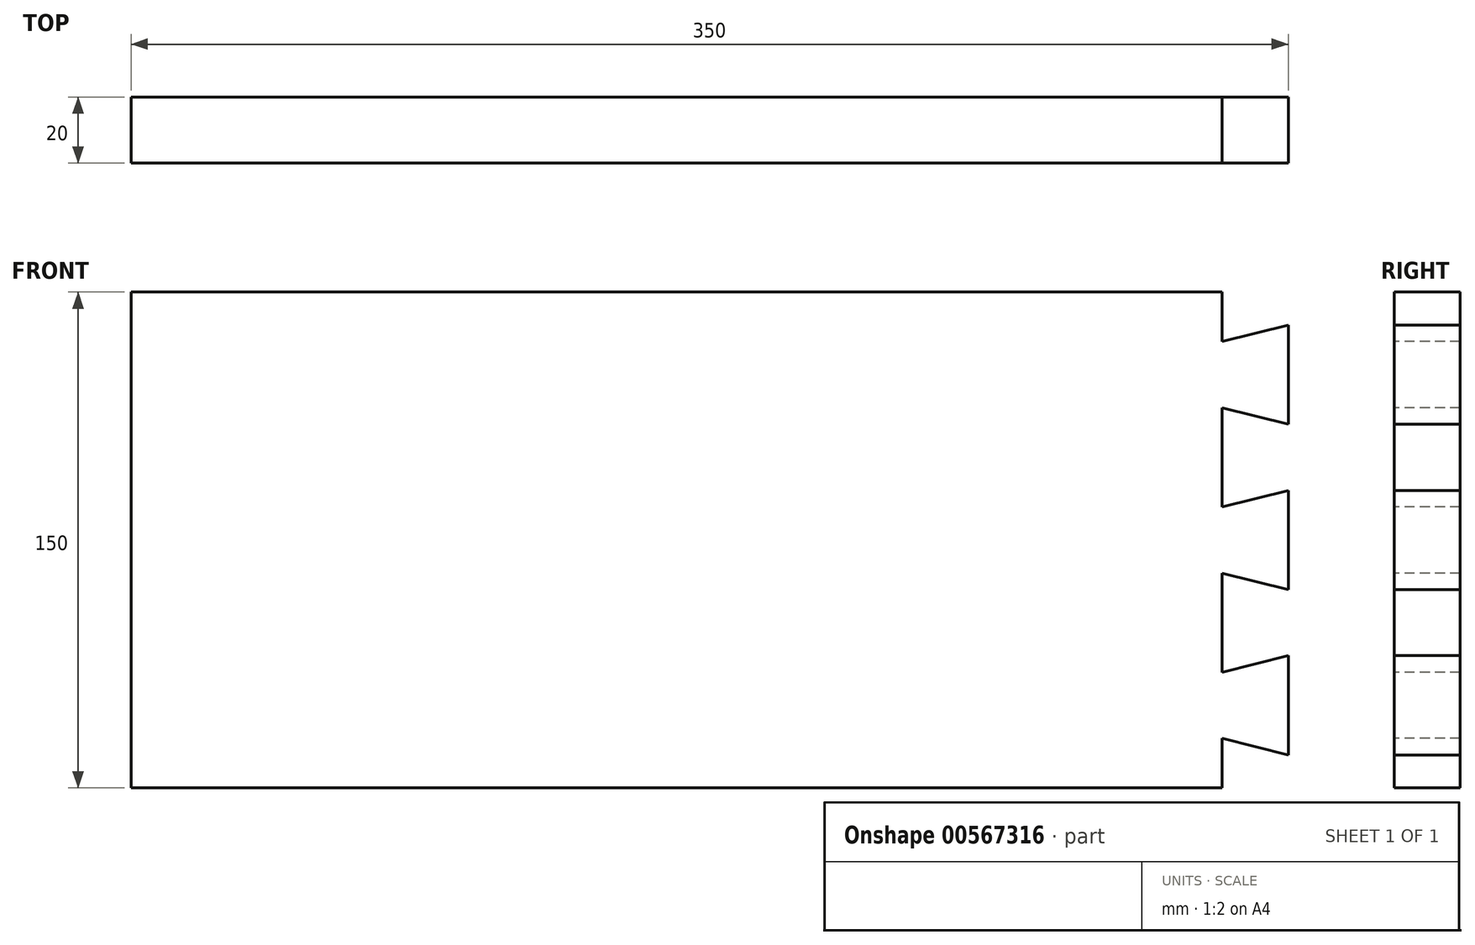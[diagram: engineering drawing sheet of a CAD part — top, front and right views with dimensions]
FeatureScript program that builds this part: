
annotation { "Feature Type Name" : "Feature", "Feature Type Description" : "" }
export const myFeature = defineFeature(function(context is Context, id is Id, definition is map)
    precondition{}
    {
        {
            var Q0;
            Q0=qCreatedBy(makeId("Front.planeOp"),FACE);
            var sketch = newSketch(context, id + "F0", { "sketchPlane" : qUnion([Q0])});
            skLineSegment(sketch, "E0.bottom", {"start": v(-187.02, 82.7) * mm, "end": v(162.98, 82.7) * mm});
            skLineSegment(sketch, "E0.top", {"start": v(-187.02, -67.3) * mm, "end": v(162.98, -67.3) * mm});
            skLineSegment(sketch, "E0.left", {"start": v(-187.02, 82.7) * mm, "end": v(-187.02, -67.3) * mm});
            skLineSegment(sketch, "E0.right", {"start": v(162.98, 82.7) * mm, "end": v(162.98, -67.3) * mm});
            skSolve(sketch);
        }
        {
            var Q0;
            Q0 = qSketchRegion(id + "F0", true);
            extrude(context, id + "F1", {"entities" : qUnion([Q0]), "depth" : 20 * mm, "offsetDistance" : 25 * mm});
        }
        {
            var Q0;
            Q0=makeQuery(id+"F1.opExtrude","SWEPT_FACE",FACE,{"disambiguationData":[OSD([sQuery(id+"F0.wireOp",EDGE,"E0.right")])]});
            var sketch = newSketch(context, id + "F2", { "sketchPlane" : qUnion([Q0])});
            skLineSegment(sketch, "E1", {"start": v(-20, 7.7) * mm, "end": v(0, 7.7) * mm});
            skLineSegment(sketch, "E2", {"start": v(-20, 22.7) * mm, "end": v(0, 17.7) * mm});
            skLineSegment(sketch, "E3", {"start": v(0, -2.3) * mm, "end": v(-20, -7.3) * mm});
            skLineSegment(sketch, "E4", {"start": v(-20, 42.7) * mm, "end": v(0, 47.7) * mm});
            skLineSegment(sketch, "E5", {"start": v(-20, 72.7) * mm, "end": v(0, 67.7) * mm});
            skLineSegment(sketch, "E6", {"start": v(-20, -27.3) * mm, "end": v(0, -32.3) * mm});
            skLineSegment(sketch, "E7", {"start": v(-20, -57.3) * mm, "end": v(0, -52.3) * mm});
            skSolve(sketch);
        }
        {
            var Q0;
            {var subQ0=sQuery(id+"F2.wireOp",EDGE,"E5");Q0=makeQuery(id+"F2.imprint","IMPRINT",FACE,{"disambiguationData":[TD([[makeQuery(id+"F2.imprint","IMPRINT",EDGE,{"derivedFrom":subQ0}),1.0]])]});}
            var Q1;
            {var subQ0=sQuery(id+"F2.wireOp",EDGE,"E2");Q1=makeQuery(id+"F2.imprint","IMPRINT",FACE,{"disambiguationData":[TD([[makeQuery(id+"F2.imprint","IMPRINT",EDGE,{"derivedFrom":subQ0}),1.0]])]});}
            var Q2;
            {var subQ0=sQuery(id+"F2.wireOp",EDGE,"E3");Q2=makeQuery(id+"F2.imprint","IMPRINT",FACE,{"disambiguationData":[TD([[makeQuery(id+"F2.imprint","IMPRINT",EDGE,{"derivedFrom":subQ0}),1.0]])]});}
            var Q3;
            {var subQ0=sQuery(id+"F2.wireOp",EDGE,"E7");Q3=makeQuery(id+"F2.imprint","IMPRINT",FACE,{"disambiguationData":[TD([[makeQuery(id+"F2.imprint","IMPRINT",EDGE,{"derivedFrom":subQ0}),-1.0]])]});}
            extrude(context, id + "F3", {"entities" : qUnion([Q0, Q1, Q2, Q3]), "operationType" : NewBodyOperationType.ADD, "oppositeDirection" : true, "depth" : 20 * mm, "offsetDistance" : 25 * mm});
        }
        {
            var Q0;
            Q0=makeQuery(id+"F1.opExtrude","CAP_FACE",FACE,{"disambiguationData":[OSD([sQuery(id+"F0.wireOp",EDGE,"E0.bottom"),sQuery(id+"F0.wireOp",EDGE,"E0.top"),sQuery(id+"F0.wireOp",EDGE,"E0.left"),sQuery(id+"F0.wireOp",EDGE,"E0.right")])],"isStart":false});
            var sketch = newSketch(context, id + "F4", { "sketchPlane" : qUnion([Q0])});
            skLineSegment(sketch, "E8", {"start": v(142.98, 82.7) * mm, "end": v(142.98, -67.3) * mm});
            skLineSegment(sketch, "E9", {"start": v(142.98, 17.7) * mm, "end": v(162.98, 22.7) * mm});
            skLineSegment(sketch, "E10", {"start": v(142.98, -2.3) * mm, "end": v(162.98, -7.3) * mm});
            skLineSegment(sketch, "E11", {"start": v(142.98, 47.7) * mm, "end": v(162.98, 42.7) * mm});
            skLineSegment(sketch, "E12", {"start": v(142.98, 67.7) * mm, "end": v(162.98, 72.7) * mm});
            skLineSegment(sketch, "E13", {"start": v(142.98, -32.3) * mm, "end": v(162.98, -27.3) * mm});
            skLineSegment(sketch, "E14", {"start": v(162.98, -57.3) * mm, "end": v(142.98, -52.3) * mm});
            skLineSegment(sketch, "E15", {"start": v(-167.02, 82.7) * mm, "end": v(-167.02, -67.3) * mm});
            skLineSegment(sketch, "E16", {"start": v(-187.02, 7.7) * mm, "end": v(-167.02, 7.7) * mm});
            skLineSegment(sketch, "E17", {"start": v(-187.02, 42.7) * mm, "end": v(-167.02, 42.7) * mm});
            skLineSegment(sketch, "E18", {"start": v(-187.02, -27.3) * mm, "end": v(-167.02, -27.3) * mm});
            skCircle(sketch, "E19", {"center": v(-177.02, 42.7) * mm, "radius": 4 * mm});
            skCircle(sketch, "E20", {"center": v(-177.02, 7.7) * mm, "radius": 4 * mm});
            skCircle(sketch, "E21", {"center": v(-177.02, -27.3) * mm, "radius": 4 * mm});
            skSolve(sketch);
        }
        {
            var Q0;
            {var subQ3=sQuery(id+"F4.wireOp",EDGE,"E12");Q0=makeQuery(id+"F4.imprint","IMPRINT",FACE,{"disambiguationData":[TD([[makeQuery(id+"F4.imprint","IMPRINT",EDGE,{"derivedFrom":subQ3}),1.0]])]});}
            var Q1;
            {var subQ0=sQuery(id+"F4.wireOp",EDGE,"E9");Q1=makeQuery(id+"F4.imprint","IMPRINT",FACE,{"disambiguationData":[TD([[makeQuery(id+"F4.imprint","IMPRINT",EDGE,{"derivedFrom":subQ0}),1.0]])]});}
            var Q2;
            {var subQ0=sQuery(id+"F4.wireOp",EDGE,"E10");Q2=makeQuery(id+"F4.imprint","IMPRINT",FACE,{"disambiguationData":[TD([[makeQuery(id+"F4.imprint","IMPRINT",EDGE,{"derivedFrom":subQ0}),-1.0]])]});}
            var Q3;
            {var subQ3=sQuery(id+"F4.wireOp",EDGE,"E14");Q3=makeQuery(id+"F4.imprint","IMPRINT",FACE,{"disambiguationData":[TD([[makeQuery(id+"F4.imprint","IMPRINT",EDGE,{"derivedFrom":subQ3}),1.0]])]});}
            extrude(context, id + "F5", {"entities" : qUnion([Q0, Q1, Q2, Q3]), "operationType" : NewBodyOperationType.REMOVE, "oppositeDirection" : true, "depth" : 20 * mm, "offsetDistance" : 25 * mm});
        }
    });
